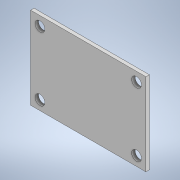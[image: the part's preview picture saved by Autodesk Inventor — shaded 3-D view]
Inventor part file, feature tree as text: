
AUTODESK INVENTOR PART (.ipt)
format: ipt  version: 2022 (Build 260153000, 153)  size: 110,080 bytes
history: native  units: mm
features: sketch x2, extrude x1, hole x1
ambient origin geometry x8: Origin, YZ Plane, XZ Plane, XY Plane, X Axis, Y Axis, Z Axis, Center Point
bodies: Solid1 (feature_tree)
feature tree (4):
  extrude  "Extrusion1"  Depth=38.1mm
  hole  "Hole1"  [1 undecoded]
  sketch  "Sketch1"  dims[d0=53.34mm d1=38.1mm]
  sketch  "Sketch2"  dims[d2=1.6mm d3=0.0mm d4=29.464mm d5=4.318mm d6=38.1mm d7=53.34mm d8=4.318mm d9=4.318mm d10=4.572mm d11=6.0mm d12=9.779mm d13=2.0mm d14=14.3117mm d15=8.0mm d16=20.594885mm]
note: 1 required parameter value undecoded (feature->parameter linkage not recoverable at this tier; creation-order binding heuristic only, values carry confidence <= 0.55)
